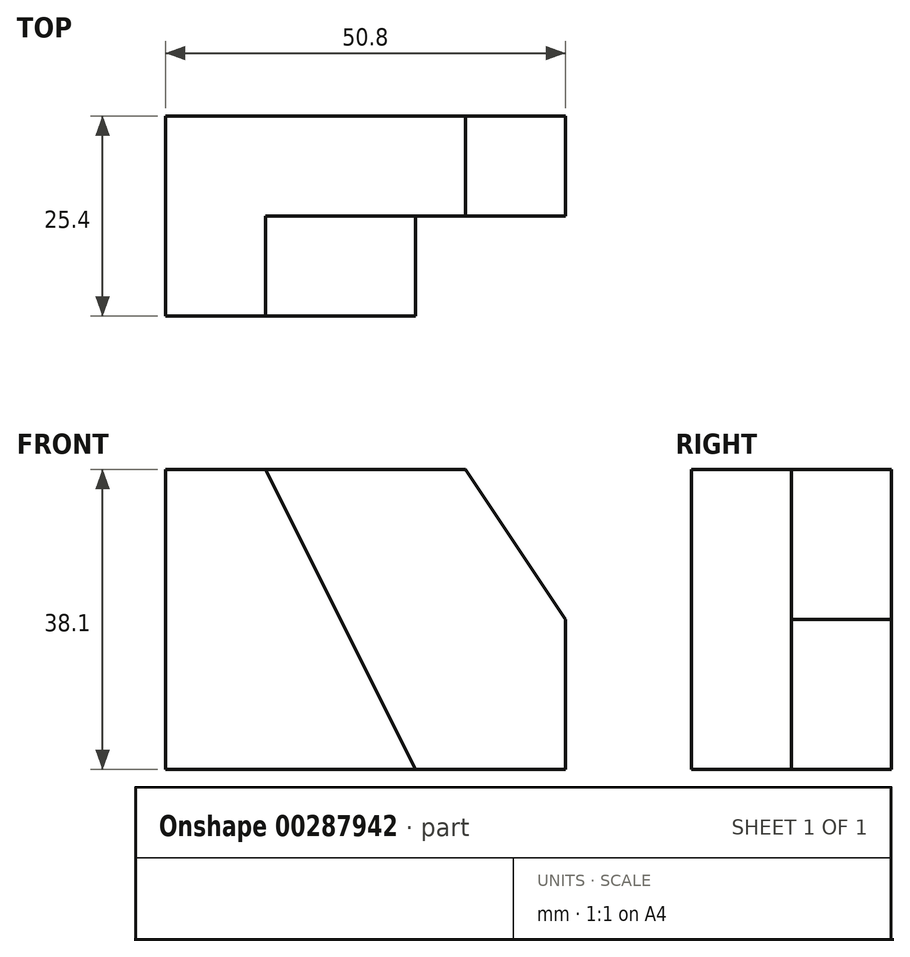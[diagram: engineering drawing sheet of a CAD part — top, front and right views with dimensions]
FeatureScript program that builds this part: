
annotation { "Feature Type Name" : "Feature", "Feature Type Description" : "" }
export const myFeature = defineFeature(function(context is Context, id is Id, definition is map)
    precondition{}
    {
        {
            var Q0;
            Q0=qCreatedBy(makeId("Front.planeOp"),FACE);
            var sketch = newSketch(context, id + "F0", { "sketchPlane" : qUnion([Q0])});
            skLineSegment(sketch, "E0.bottom", {"start": v(-86.56, 64.84) * mm, "end": v(-35.76, 64.84) * mm});
            skLineSegment(sketch, "E0.top", {"start": v(-86.56, 26.74) * mm, "end": v(-35.76, 26.74) * mm});
            skLineSegment(sketch, "E0.left", {"start": v(-86.56, 64.84) * mm, "end": v(-86.56, 26.74) * mm});
            skLineSegment(sketch, "E0.right", {"start": v(-35.76, 64.84) * mm, "end": v(-35.76, 26.74) * mm});
            skSolve(sketch);
        }
        {
            var Q0;
            Q0=makeQuery(id+"F0.imprint","IMPRINT",FACE,{"disambiguationData":[TD([[makeQuery(id+"F0.imprint","IMPRINT",EDGE,{"derivedFrom":sQuery(id+"F0.wireOp",EDGE,"E0.bottom")}),-1.0]])]});
            extrude(context, id + "F1", {"entities" : qUnion([Q0]), "depth" : 25.4 * mm, "offsetDistance" : 25.4 * mm});
        }
        {
            var Q0;
            Q0=makeQuery(id+"F1.opExtrude","CAP_FACE",FACE,{"disambiguationData":[OSD([sQuery(id+"F0.wireOp",EDGE,"E0.bottom"),sQuery(id+"F0.wireOp",EDGE,"E0.top"),sQuery(id+"F0.wireOp",EDGE,"E0.left"),sQuery(id+"F0.wireOp",EDGE,"E0.right")])],"isStart":false});
            var sketch = newSketch(context, id + "F2", { "sketchPlane" : qUnion([Q0])});
            skLineSegment(sketch, "E1", {"start": v(-54.8, 26.74) * mm, "end": v(-73.86, 64.84) * mm});
            skSolve(sketch);
        }
        {
            var Q0;
            Q0 = qSketchRegion(id + "F2", true);
            var Q1;
            {var subQ0=sQuery(id+"F2.wireOp",EDGE,"E1");Q1=makeQuery(id+"F2.imprint","IMPRINT",FACE,{"disambiguationData":[TD([[makeQuery(id+"F2.imprint","IMPRINT",EDGE,{"derivedFrom":subQ0}),-1.0]])]});}
            extrude(context, id + "F3", {"entities" : qUnion([Q0, Q1]), "operationType" : NewBodyOperationType.REMOVE, "oppositeDirection" : true, "depth" : 12.7 * mm, "offsetDistance" : 25.4 * mm});
        }
        {
            var Q0;
            Q0=makeQuery(id+"F3.boolean.opBoolean","COPY",FACE,{"derivedFrom":makeQuery(id+"F3.opExtrude","CAP_FACE",FACE,{"disambiguationData":[OSD([sQuery(id+"F0.wireOp",EDGE,"E0.bottom"),sQuery(id+"F0.wireOp",EDGE,"E0.top"),sQuery(id+"F0.wireOp",EDGE,"E0.right"),sQuery(id+"F2.wireOp",EDGE,"E1")])],"isStart":false})});
            var sketch = newSketch(context, id + "F4", { "sketchPlane" : qUnion([Q0])});
            skLineSegment(sketch, "E2", {"start": v(-35.76, 45.8) * mm, "end": v(-48.46, 64.84) * mm});
            skSolve(sketch);
        }
        {
            var Q0;
            {var subQ0=sQuery(id+"F4.wireOp",EDGE,"E2");Q0=makeQuery(id+"F4.imprint","IMPRINT",FACE,{"disambiguationData":[TD([[makeQuery(id+"F4.imprint","IMPRINT",EDGE,{"derivedFrom":subQ0}),-1.0]])]});}
            extrude(context, id + "F5", {"entities" : qUnion([Q0]), "operationType" : NewBodyOperationType.REMOVE, "oppositeDirection" : true, "depth" : 25.4 * mm, "offsetDistance" : 25.4 * mm});
        }
    });
